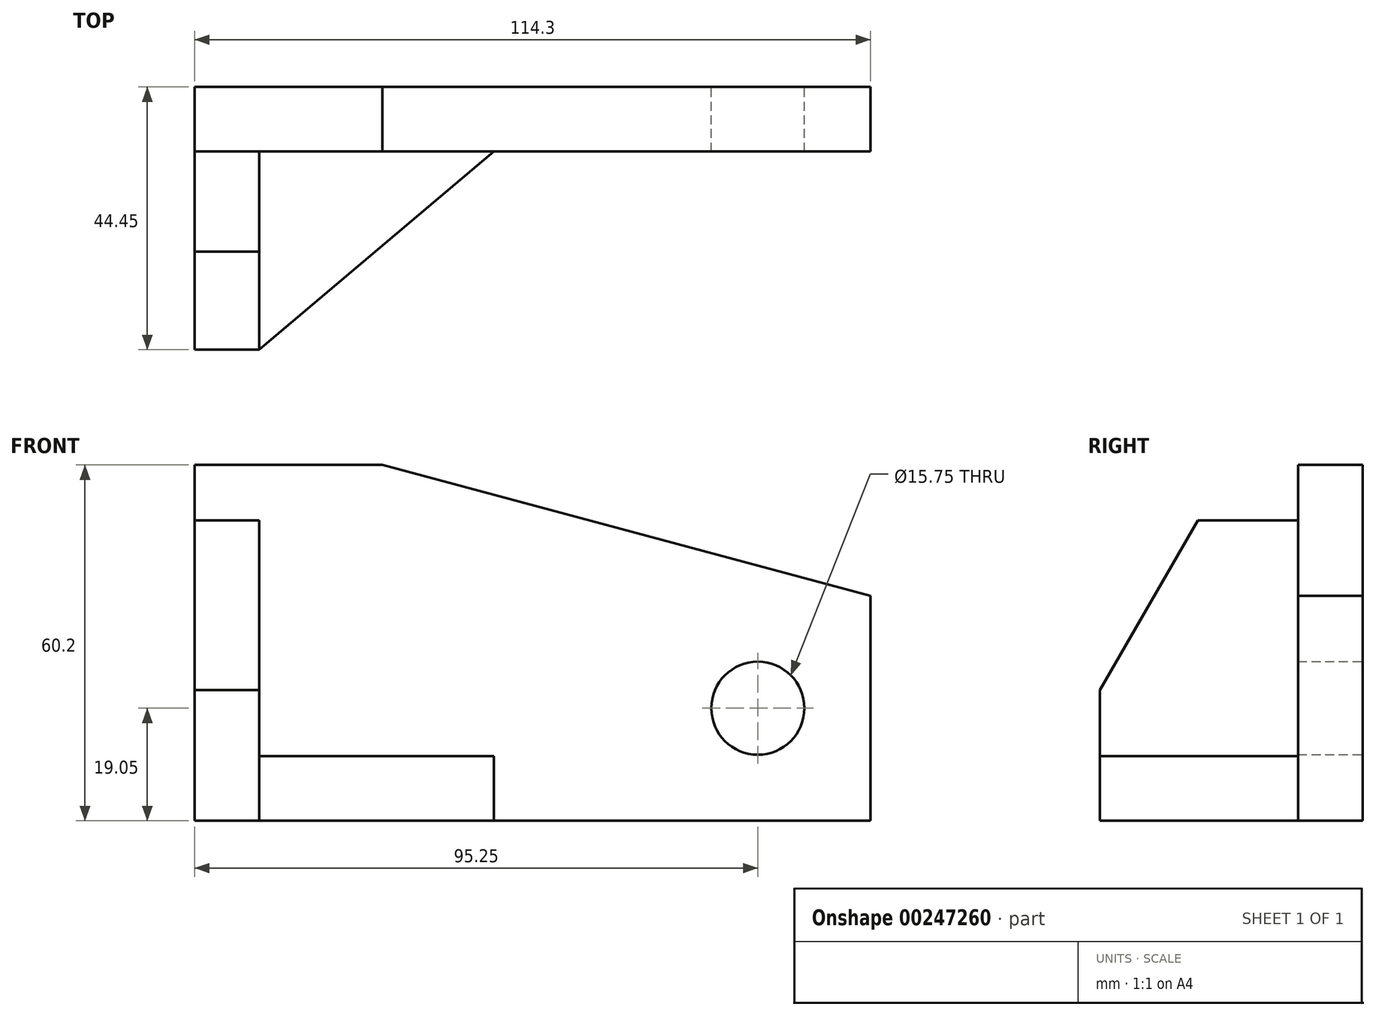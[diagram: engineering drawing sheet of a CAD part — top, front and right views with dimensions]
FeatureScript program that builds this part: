
annotation { "Feature Type Name" : "Feature", "Feature Type Description" : "" }
export const myFeature = defineFeature(function(context is Context, id is Id, definition is map)
    precondition{}
    {
        {
            var Q0;
            Q0=qCreatedBy(makeId("Front.planeOp"),FACE);
            var sketch = newSketch(context, id + "F0", { "sketchPlane" : qUnion([Q0])});
            skLineSegment(sketch, "E0.left", {"start": v(114.3, 38.08) * mm, "end": v(114.3, 0) * mm});
            skLineSegment(sketch, "E0.right", {"start": v(0, 60.2) * mm, "end": v(0, 0) * mm});
            skPoint(sketch, "E0.middle", {"position": v(0, 0) * mm});
            skLineSegment(sketch, "E1", {"start": v(114.3, 38.08) * mm, "end": v(31.75, 60.2) * mm});
            skLineSegment(sketch, "E2", {"start": v(0, 60.2) * mm, "end": v(31.75, 60.2) * mm});
            skLineSegment(sketch, "E3", {"start": v(31.75, 60.2) * mm, "end": v(114.3, 60.2) * mm, "construction": true});
            skLineSegment(sketch, "E4", {"start": v(114.3, 0) * mm, "end": v(0, 0) * mm});
            skCircle(sketch, "E5", {"center": v(95.25, 19.05) * mm, "radius": 7.87 * mm});
            skSolve(sketch);
        }
        {
            var Q0;
            Q0=qCreatedBy(makeId("Right.planeOp"),FACE);
            var sketch = newSketch(context, id + "F1", { "sketchPlane" : qUnion([Q0])});
            skLineSegment(sketch, "E6", {"start": v(0, 0) * mm, "end": v(0, 50.8) * mm});
            skLineSegment(sketch, "E7", {"start": v(0, 50.8) * mm, "end": v(-10.34, 50.8) * mm});
            skLineSegment(sketch, "E8", {"start": v(0, 0) * mm, "end": v(-44.45, 0) * mm});
            skLineSegment(sketch, "E9", {"start": v(-44.45, 0) * mm, "end": v(-44.45, 22.1) * mm});
            skLineSegment(sketch, "E10", {"start": v(-44.45, 22.1) * mm, "end": v(-27.88, 50.8) * mm});
            skLineSegment(sketch, "E11", {"start": v(-10.34, 50.8) * mm, "end": v(-27.88, 50.8) * mm});
            skSolve(sketch);
        }
        {
            var Q0;
            Q0=qCreatedBy(makeId("Top.planeOp"),FACE);
            var sketch = newSketch(context, id + "F2", { "sketchPlane" : qUnion([Q0])});
            skLineSegment(sketch, "E12", {"start": v(0, 0) * mm, "end": v(63.5, 0) * mm});
            skLineSegment(sketch, "E13", {"start": v(0, 0) * mm, "end": v(0, -44.45) * mm});
            skLineSegment(sketch, "E14", {"start": v(0, -44.45) * mm, "end": v(10.92, -44.45) * mm});
            skLineSegment(sketch, "E15", {"start": v(63.5, 0) * mm, "end": v(10.92, -44.45) * mm});
            skSolve(sketch);
        }
        {
            var Q0;
            Q0=makeQuery(id+"F0.imprint","IMPRINT",FACE,{"disambiguationData":[TD([[makeQuery(id+"F0.imprint","IMPRINT",EDGE,{"derivedFrom":sQuery(id+"F0.wireOp",EDGE,"E0.right")}),1.0]])]});
            extrude(context, id + "F3", {"entities" : qUnion([Q0]), "depth" : 10.92 * mm});
        }
        {
            var Q0;
            Q0 = qSketchRegion(id + "F1", true);
            extrude(context, id + "F4", {"entities" : qUnion([Q0]), "operationType" : NewBodyOperationType.ADD, "depth" : 10.92 * mm});
        }
        {
            var Q0;
            Q0 = qSketchRegion(id + "F2", true);
            extrude(context, id + "F5", {"entities" : qUnion([Q0]), "operationType" : NewBodyOperationType.ADD, "depth" : 10.92 * mm});
        }
    });
